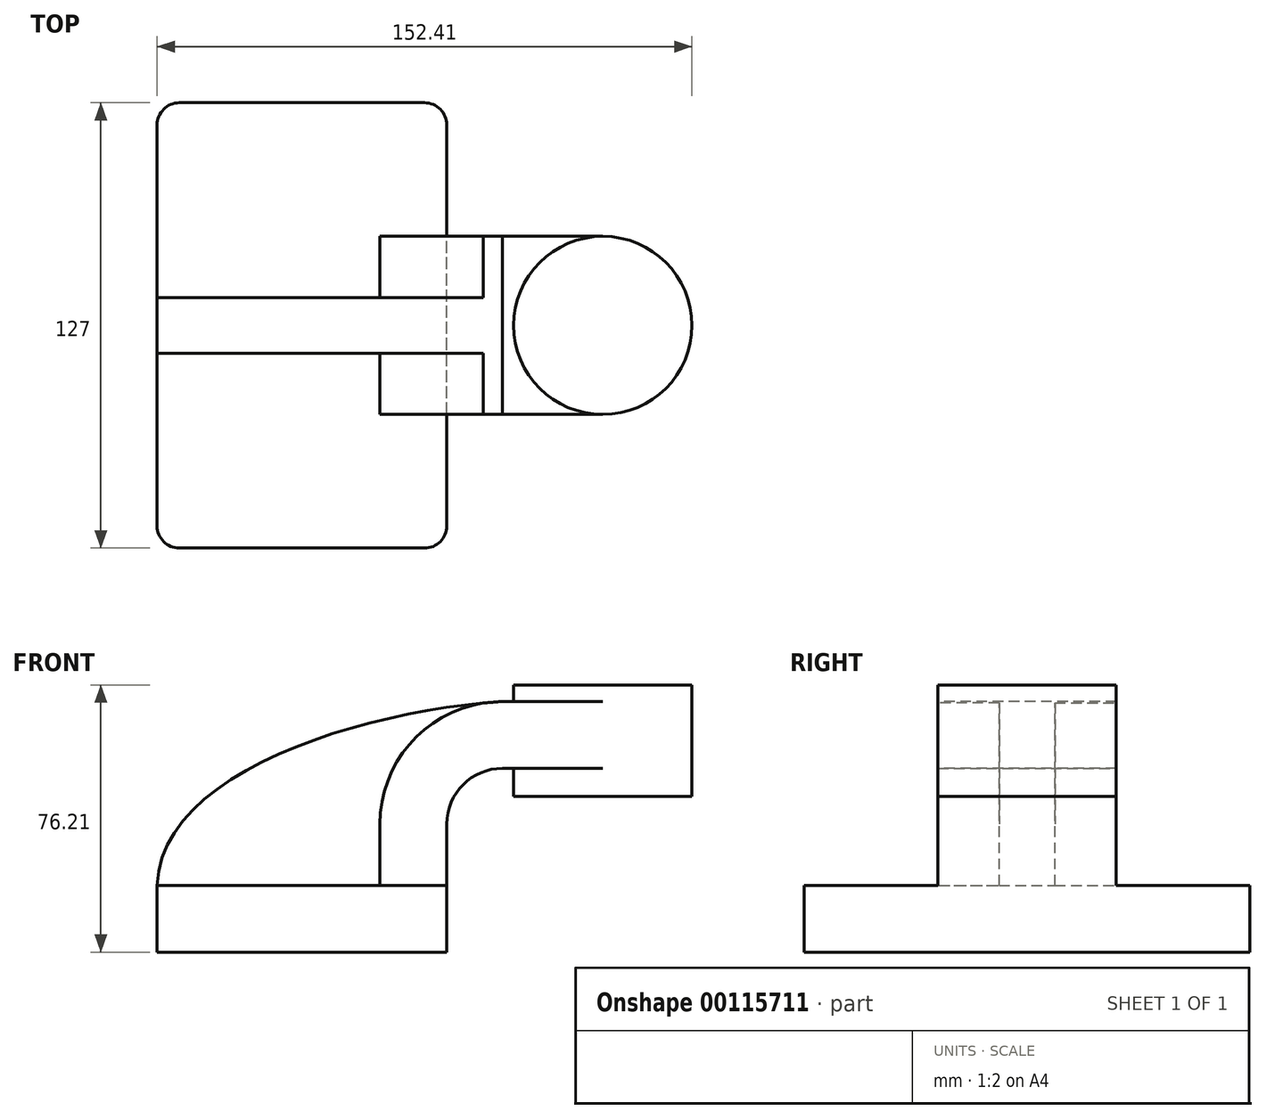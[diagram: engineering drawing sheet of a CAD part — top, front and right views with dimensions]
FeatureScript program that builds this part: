
annotation { "Feature Type Name" : "Feature", "Feature Type Description" : "" }
export const myFeature = defineFeature(function(context is Context, id is Id, definition is map)
    precondition{}
    {
        {
            var Q0;
            Q0=qCreatedBy(makeId("Front.planeOp"),FACE);
            var sketch = newSketch(context, id + "F0", { "sketchPlane" : qUnion([Q0])});
            skLineSegment(sketch, "E0.bottom", {"start": v(41.28, -9.52) * mm, "end": v(-41.27, -9.53) * mm});
            skLineSegment(sketch, "E0.top", {"start": v(41.27, 9.53) * mm, "end": v(-41.28, 9.53) * mm});
            skLineSegment(sketch, "E0.left", {"start": v(41.28, -9.52) * mm, "end": v(41.27, 9.53) * mm});
            skLineSegment(sketch, "E0.right", {"start": v(-41.27, -9.53) * mm, "end": v(-41.28, 9.53) * mm});
            skPoint(sketch, "E0.middle", {"position": v(0, 0) * mm});
            skLineSegment(sketch, "E1.bottom", {"start": v(111.12, 34.93) * mm, "end": v(60.32, 34.93) * mm});
            skLineSegment(sketch, "E1.top", {"start": v(111.12, 66.68) * mm, "end": v(60.32, 66.68) * mm});
            skLineSegment(sketch, "E1.left", {"start": v(111.12, 34.93) * mm, "end": v(111.12, 66.68) * mm});
            skLineSegment(sketch, "E1.right", {"start": v(60.32, 34.93) * mm, "end": v(60.32, 66.68) * mm});
            skPoint(sketch, "E1.middle", {"position": v(85.72, 50.8) * mm});
            skLineSegment(sketch, "E2", {"start": v(41.27, 9.53) * mm, "end": v(41.27, 27) * mm});
            skArc(sketch, "E3", {"start": v(41.27, 27) * mm, "mid": v(45.92, 38.23) * mm, "end": v(57.15, 42.88) * mm});
            skLineSegment(sketch, "E4", {"start": v(57.15, 42.88) * mm, "end": v(85.72, 42.88) * mm});
            skLineSegment(sketch, "E5.0", {"start": v(57.15, 61.93) * mm, "end": v(85.72, 61.93) * mm});
            skArc(sketch, "E5.1", {"start": v(22.22, 27) * mm, "mid": v(32.45, 51.7) * mm, "end": v(57.15, 61.93) * mm});
            skLineSegment(sketch, "E5.2", {"start": v(22.22, 9.53) * mm, "end": v(22.22, 27) * mm});
            skLineSegment(sketch, "E6", {"start": v(85.72, 66.68) * mm, "end": v(85.72, 34.93) * mm});
            skFitSpline(sketch, "E7", {"points": [v(-41.28, 9.53) * mm, v(57.15, 61.93) * mm], "startDerivative": vector(3.13, 97.8) * mm, "endDerivative": vector(117.99, 7.56) * mm});
            skSolve(sketch);
        }
        {
            var Q0;
            Q0=makeQuery(id+"F0.imprint","IMPRINT",FACE,{"disambiguationData":[TD([[makeQuery(id+"F0.imprint","IMPRINT",EDGE,{"derivedFrom":sQuery(id+"F0.wireOp",EDGE,"E0.bottom")}),-1.0]])]});
            extrude(context, id + "F1", {"entities" : qUnion([Q0]), "endBound" : BoundingType.SYMMETRIC, "depth" : 127 * mm});
        }
        {
            var Q0;
            {var subQ1=sQuery(id+"F0.wireOp",EDGE,"E2");Q0=makeQuery(id+"F0.imprint","IMPRINT",FACE,{"disambiguationData":[TD([[makeQuery(id+"F0.imprint","IMPRINT",EDGE,{"derivedFrom":subQ1}),1.0]])]});}
            var Q1;
            {var subQ0=sQuery(id+"F0.wireOp",EDGE,"E4");var subQ1=sQuery(id+"F0.wireOp",EDGE,"E1.right");var subQ2=makeQuery(id+"F0.imprint","INTERSECT",VERTEX,{"derivedFrom":[subQ1,subQ0]});Q1=makeQuery(id+"F0.imprint","IMPRINT",FACE,{"disambiguationData":[TD([[makeQuery(id+"F0.imprint","IMPRINT",EDGE,{"disambiguationData":[TD([[subQ2,-1.0]])],"derivedFrom":subQ1}),-1.0]])]});}
            extrude(context, id + "F2", {"entities" : qUnion([Q0, Q1]), "operationType" : NewBodyOperationType.ADD, "endBound" : BoundingType.SYMMETRIC, "depth" : 50.8 * mm});
        }
        {
            var Q0;
            {var subQ3=sQuery(id+"F0.wireOp",EDGE,"E5.2");Q0=makeQuery(id+"F0.imprint","IMPRINT",FACE,{"disambiguationData":[TD([[makeQuery(id+"F0.imprint","IMPRINT",EDGE,{"derivedFrom":subQ3}),1.0]])]});}
            extrude(context, id + "F3", {"entities" : qUnion([Q0]), "operationType" : NewBodyOperationType.ADD, "endBound" : BoundingType.SYMMETRIC, "depth" : 15.88 * mm});
        }
        {
            var Q0;
            {var subQ0=sQuery(id+"F0.wireOp",EDGE,"E1.left");Q0=makeQuery(id+"F0.imprint","IMPRINT",FACE,{"disambiguationData":[TD([[makeQuery(id+"F0.imprint","IMPRINT",EDGE,{"derivedFrom":subQ0}),1.0]])]});}
            var Q1;
            Q1=sQuery(id+"F0.wireOp",EDGE,"E6");
            revolve(context, id + "F4", {"operationType" : NewBodyOperationType.ADD, "entities" : qUnion([Q0]), "axis" : qUnion([Q1]), "revolveType" : RevolveType.FULL});
        }
        {
            var Q0;
            Q0=makeQuery(id+"F1.opExtrude","CAP_EDGE",EDGE,{"disambiguationData":[OSD([sQuery(id+"F0.wireOp",EDGE,"E0.left")])],"isStart":false});
            var Q1;
            Q1=makeQuery(id+"F1.opExtrude","CAP_EDGE",EDGE,{"disambiguationData":[OSD([sQuery(id+"F0.wireOp",EDGE,"E0.left")])],"isStart":true});
            var Q2;
            Q2=makeQuery(id+"F1.opExtrude","CAP_EDGE",EDGE,{"disambiguationData":[OSD([sQuery(id+"F0.wireOp",EDGE,"E0.right")])],"isStart":true});
            var Q3;
            Q3=makeQuery(id+"F1.opExtrude","CAP_EDGE",EDGE,{"disambiguationData":[OSD([sQuery(id+"F0.wireOp",EDGE,"E0.right")])],"isStart":false});
            fillet(context, id + "F5", {"entities" : qUnion([Q0, Q1, Q2, Q3]), "radius" : 6.35 * mm, "tangentPropagation" : true, "allowEdgeOverflow" : false});
        }
    });
